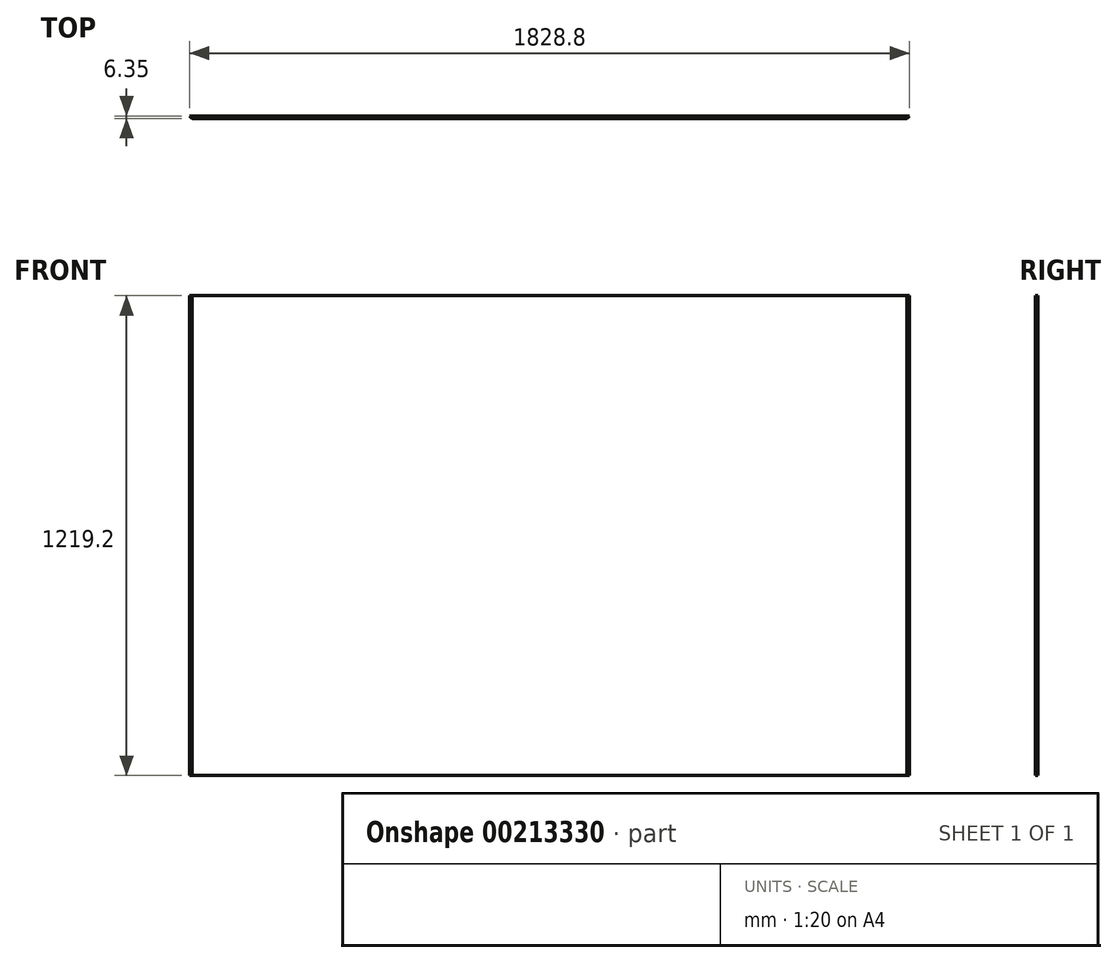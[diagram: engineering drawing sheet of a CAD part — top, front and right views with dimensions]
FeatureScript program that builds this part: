
annotation { "Feature Type Name" : "Feature", "Feature Type Description" : "" }
export const myFeature = defineFeature(function(context is Context, id is Id, definition is map)
    precondition{}
    {
        {
            var Q0;
            Q0=qCreatedBy(makeId("Front.planeOp"),FACE);
            var sketch = newSketch(context, id + "F0", { "sketchPlane" : qUnion([Q0])});
            skLineSegment(sketch, "E0.bottom", {"start": v(914.4, -609.6) * mm, "end": v(-914.4, -609.6) * mm});
            skLineSegment(sketch, "E0.top", {"start": v(914.4, 609.6) * mm, "end": v(-914.4, 609.6) * mm});
            skLineSegment(sketch, "E0.left", {"start": v(914.4, -609.6) * mm, "end": v(914.4, 609.6) * mm});
            skLineSegment(sketch, "E0.right", {"start": v(-914.4, -609.6) * mm, "end": v(-914.4, 609.6) * mm});
            skPoint(sketch, "E0.middle", {"position": v(0, 0) * mm});
            skSolve(sketch);
        }
        {
            var Q0;
            Q0=makeQuery(id+"F0.imprint","IMPRINT",FACE,{"disambiguationData":[TD([[makeQuery(id+"F0.imprint","IMPRINT",EDGE,{"derivedFrom":sQuery(id+"F0.wireOp",EDGE,"E0.bottom")}),-1.0]])]});
            extrude(context, id + "F1", {"entities" : qUnion([Q0]), "endBound" : BoundingType.SYMMETRIC, "depth" : 6.35 * mm});
        }
        {
            var Q0;
            Q0=makeQuery(id+"F1.opExtrude","CAP_EDGE",EDGE,{"disambiguationData":[OSD([sQuery(id+"F0.wireOp",EDGE,"E0.right")])],"isStart":false});
            chamfer(context, id + "F2", {"entities" : qUnion([Q0]), "width" : 6.35 * mm, "tangentPropagation" : true});
        }
        {
            var Q0;
            Q0=makeQuery(id+"F1.opExtrude","CAP_EDGE",EDGE,{"disambiguationData":[OSD([sQuery(id+"F0.wireOp",EDGE,"E0.left")])],"isStart":false});
            chamfer(context, id + "F3", {"entities" : qUnion([Q0]), "width" : 6.35 * mm, "tangentPropagation" : true});
        }
    });
